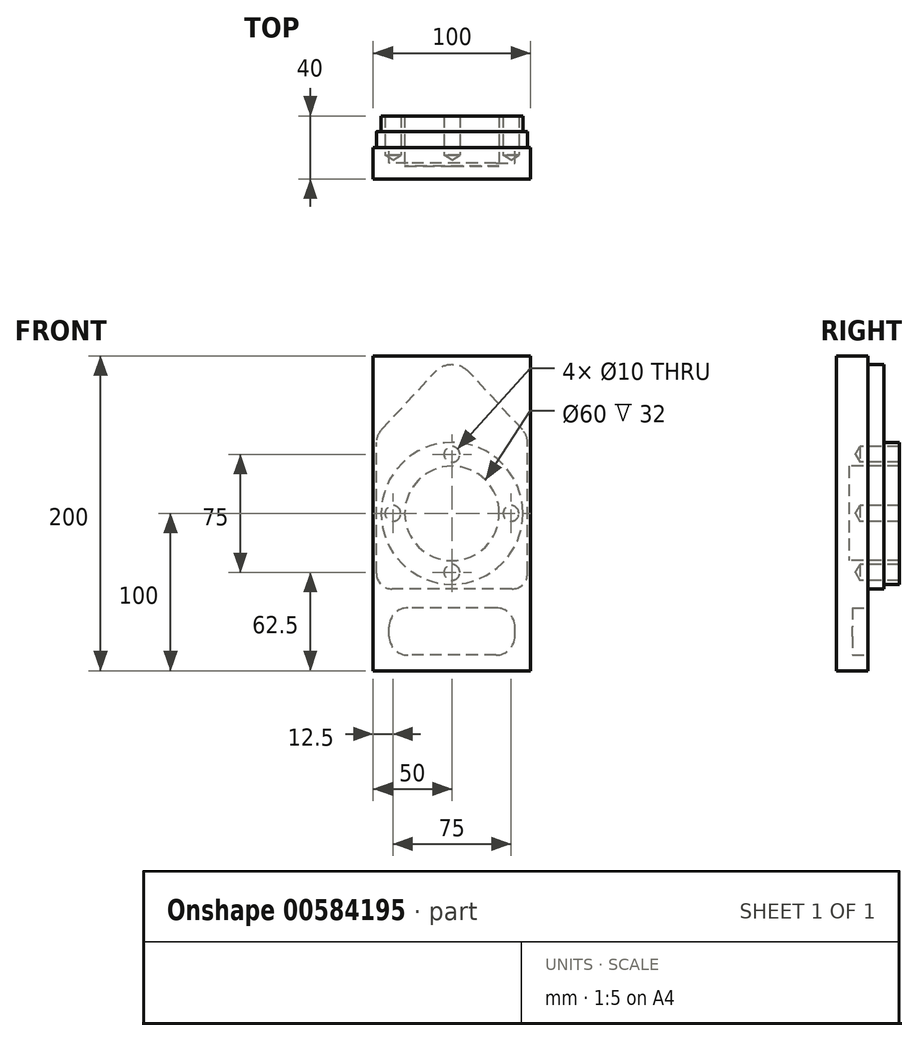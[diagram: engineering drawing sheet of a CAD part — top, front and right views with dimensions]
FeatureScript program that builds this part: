
annotation { "Feature Type Name" : "Feature", "Feature Type Description" : "" }
export const myFeature = defineFeature(function(context is Context, id is Id, definition is map)
    precondition{}
    {
        {
            var Q0;
            Q0=qCreatedBy(makeId("Front.planeOp"),FACE);
            var sketch = newSketch(context, id + "F0", { "sketchPlane" : qUnion([Q0])});
            skLineSegment(sketch, "E0.bottom", {"start": v(50, -100) * mm, "end": v(-50, -100) * mm});
            skLineSegment(sketch, "E0.top", {"start": v(50, 100) * mm, "end": v(-50, 100) * mm});
            skLineSegment(sketch, "E0.left", {"start": v(50, -100) * mm, "end": v(50, 100) * mm});
            skLineSegment(sketch, "E0.right", {"start": v(-50, -100) * mm, "end": v(-50, 100) * mm});
            skSolve(sketch);
        }
        {
            var Q0;
            Q0=makeQuery(id+"F0.imprint","IMPRINT",FACE,{"disambiguationData":[TD([[makeQuery(id+"F0.imprint","IMPRINT",EDGE,{"derivedFrom":sQuery(id+"F0.wireOp",EDGE,"E0.bottom")}),-1.0]])]});
            extrude(context, id + "F1", {"entities" : qUnion([Q0]), "depth" : 20 * mm, "offsetDistance" : 25 * mm});
        }
        {
            var Q0;
            Q0=makeQuery(id+"F1.opExtrude","CAP_FACE",FACE,{"disambiguationData":[OSD([sQuery(id+"F0.wireOp",EDGE,"E0.bottom"),sQuery(id+"F0.wireOp",EDGE,"E0.top"),sQuery(id+"F0.wireOp",EDGE,"E0.left"),sQuery(id+"F0.wireOp",EDGE,"E0.right")])],"isStart":true});
            var sketch = newSketch(context, id + "F2", { "sketchPlane" : qUnion([Q0])});
            skLineSegment(sketch, "E1.bottom", {"start": v(-28, -90) * mm, "end": v(28, -90) * mm});
            skLineSegment(sketch, "E1.top", {"start": v(-28, -60) * mm, "end": v(28, -60) * mm});
            skLineSegment(sketch, "E1.left", {"start": v(-40, -78) * mm, "end": v(-40, -72) * mm});
            skLineSegment(sketch, "E1.right", {"start": v(40, -78) * mm, "end": v(40, -72) * mm});
            skLineSegment(sketch, "E2", {"start": v(-38, -48) * mm, "end": v(38, -48) * mm});
            skLineSegment(sketch, "E3", {"start": v(-48, -38) * mm, "end": v(-48, 45) * mm});
            skLineSegment(sketch, "E4", {"start": v(48, -38) * mm, "end": v(48, 45) * mm});
            skLineSegment(sketch, "E5", {"start": v(-44.8, 53.16) * mm, "end": v(-11, 89.62) * mm});
            skLineSegment(sketch, "E6", {"start": v(44.8, 53.16) * mm, "end": v(11, 89.62) * mm});
            skArc(sketch, "E7", {"start": v(-48, -38) * mm, "mid": v(-45.07, -45.07) * mm, "end": v(-38, -48) * mm});
            skArc(sketch, "E8", {"start": v(38, -48) * mm, "mid": v(45.07, -45.07) * mm, "end": v(48, -38) * mm});
            skArc(sketch, "E9", {"start": v(-44.8, 53.16) * mm, "mid": v(-47.17, 49.38) * mm, "end": v(-48, 45) * mm});
            skArc(sketch, "E10", {"start": v(48, 45) * mm, "mid": v(47.17, 49.38) * mm, "end": v(44.8, 53.16) * mm});
            skArc(sketch, "E11", {"start": v(11, 89.62) * mm, "mid": v(0, 94.42) * mm, "end": v(-11, 89.62) * mm});
            skPoint(sketch, "E12.visualSharp", {"position": v(-40, -90) * mm});
            skArc(sketch, "E12.filletArc", {"start": v(-40, -78) * mm, "mid": v(-36.49, -86.49) * mm, "end": v(-28, -90) * mm});
            skPoint(sketch, "E13.visualSharp", {"position": v(-40, -60) * mm});
            skArc(sketch, "E13.filletArc", {"start": v(-28, -60) * mm, "mid": v(-36.49, -63.51) * mm, "end": v(-40, -72) * mm});
            skPoint(sketch, "E14.visualSharp", {"position": v(40, -60) * mm});
            skArc(sketch, "E14.filletArc", {"start": v(40, -72) * mm, "mid": v(36.49, -63.51) * mm, "end": v(28, -60) * mm});
            skPoint(sketch, "E15.visualSharp", {"position": v(40, -90) * mm});
            skArc(sketch, "E15.filletArc", {"start": v(28, -90) * mm, "mid": v(36.49, -86.49) * mm, "end": v(40, -78) * mm});
            skSolve(sketch);
        }
        {
            var Q0;
            Q0=makeQuery(id+"F2.imprint","IMPRINT",FACE,{"disambiguationData":[TD([[makeQuery(id+"F2.imprint","IMPRINT",EDGE,{"derivedFrom":sQuery(id+"F2.wireOp",EDGE,"E2")}),1.0]])]});
            extrude(context, id + "F3", {"entities" : qUnion([Q0]), "operationType" : NewBodyOperationType.ADD, "depth" : 10 * mm, "offsetDistance" : 25 * mm});
        }
        {
            var Q0;
            Q0=makeQuery(id+"F2.imprint","IMPRINT",FACE,{"disambiguationData":[TD([[makeQuery(id+"F2.imprint","IMPRINT",EDGE,{"derivedFrom":sQuery(id+"F2.wireOp",EDGE,"E1.bottom")}),1.0]])]});
            extrude(context, id + "F4", {"entities" : qUnion([Q0]), "operationType" : NewBodyOperationType.REMOVE, "oppositeDirection" : true, "depth" : 10 * mm, "offsetDistance" : 25 * mm});
        }
        {
            var Q0;
            Q0=makeQuery(id+"F3.opExtrude","CAP_FACE",FACE,{"disambiguationData":[OSD([sQuery(id+"F2.wireOp",EDGE,"E2"),sQuery(id+"F2.wireOp",EDGE,"E3"),sQuery(id+"F2.wireOp",EDGE,"E4"),sQuery(id+"F2.wireOp",EDGE,"E5"),sQuery(id+"F2.wireOp",EDGE,"E6"),sQuery(id+"F2.wireOp",EDGE,"E7"),sQuery(id+"F2.wireOp",EDGE,"E8"),sQuery(id+"F2.wireOp",EDGE,"E9"),sQuery(id+"F2.wireOp",EDGE,"E10"),sQuery(id+"F2.wireOp",EDGE,"E11")])],"isStart":false});
            var sketch = newSketch(context, id + "F5", { "sketchPlane" : qUnion([Q0])});
            skCircle(sketch, "E16", {"center": v(0, 0) * mm, "radius": 45 * mm});
            skCircle(sketch, "E17", {"center": v(0, 0) * mm, "radius": 37.5 * mm, "construction": true});
            skCircle(sketch, "E18", {"center": v(0, 0) * mm, "radius": 30 * mm});
            skCircle(sketch, "E19", {"center": v(-37.5, 0) * mm, "radius": 5 * mm});
            skCircle(sketch, "E20", {"center": v(0, 37.5) * mm, "radius": 5 * mm});
            skCircle(sketch, "E21", {"center": v(37.5, 0) * mm, "radius": 5 * mm});
            skCircle(sketch, "E22", {"center": v(0, -37.5) * mm, "radius": 5 * mm});
            skSolve(sketch);
        }
        {
            var Q0;
            Q0=makeQuery(id+"F5.imprint","IMPRINT",FACE,{"disambiguationData":[TD([[makeQuery(id+"F5.imprint","IMPRINT",EDGE,{"derivedFrom":sQuery(id+"F5.wireOp",EDGE,"E16")}),1.0]])]});
            extrude(context, id + "F6", {"entities" : qUnion([Q0]), "operationType" : NewBodyOperationType.ADD, "depth" : 10 * mm, "offsetDistance" : 25 * mm});
        }
        {
            var Q0;
            Q0=makeQuery(id+"F6.boolean.opBoolean","SPLIT",FACE,{"disambiguationData":[TD([makeQuery(id+"F6.opExtrude","SWEPT_FACE",FACE,{"disambiguationData":[OSD([sQuery(id+"F5.wireOp",EDGE,"E18")])]})])],"derivedFrom":makeQuery(id+"F3.opExtrude","CAP_FACE",FACE,{"disambiguationData":[OSD([sQuery(id+"F2.wireOp",EDGE,"E2"),sQuery(id+"F2.wireOp",EDGE,"E3"),sQuery(id+"F2.wireOp",EDGE,"E4"),sQuery(id+"F2.wireOp",EDGE,"E5"),sQuery(id+"F2.wireOp",EDGE,"E6"),sQuery(id+"F2.wireOp",EDGE,"E7"),sQuery(id+"F2.wireOp",EDGE,"E8"),sQuery(id+"F2.wireOp",EDGE,"E9"),sQuery(id+"F2.wireOp",EDGE,"E10"),sQuery(id+"F2.wireOp",EDGE,"E11")])],"isStart":false})});
            extrude(context, id + "F7", {"entities" : qUnion([Q0]), "operationType" : NewBodyOperationType.REMOVE, "oppositeDirection" : true, "depth" : 22 * mm, "offsetDistance" : 25 * mm});
        }
        {
            var Q0;
            Q0=sQuery(id+"F5.wireOp",VERTEX,"E19.center");
            var Q1;
            Q1=sQuery(id+"F5.wireOp",VERTEX,"E20.center");
            var Q2;
            Q2=sQuery(id+"F5.wireOp",VERTEX,"E21.center");
            var Q3;
            Q3=sQuery(id+"F5.wireOp",VERTEX,"E22.center");
            var Q4;
            Q4=makeQuery(id+"F1.opExtrude","SWEPT_BODY",BODY,{"disambiguationData":[OSD([sQuery(id+"F0.wireOp",EDGE,"E0.bottom"),sQuery(id+"F0.wireOp",EDGE,"E0.top"),sQuery(id+"F0.wireOp",EDGE,"E0.left"),sQuery(id+"F0.wireOp",EDGE,"E0.right")])]});
            hole(context, id + "F8", {"style" : HoleStyle.SIMPLE, "endStyle" : HoleEndStyle.BLIND, "holeDiameter" : 10 * mm, "majorDiameter" : 5 * mm, "holeDepth" : 15 * mm, "isTappedThrough" : true, "tappedDepth" : 12 * mm, "tapClearance" : 3, "locations" : qUnion([Q0, Q1, Q2, Q3]), "scope" : qUnion([Q4])});
        }
    });
